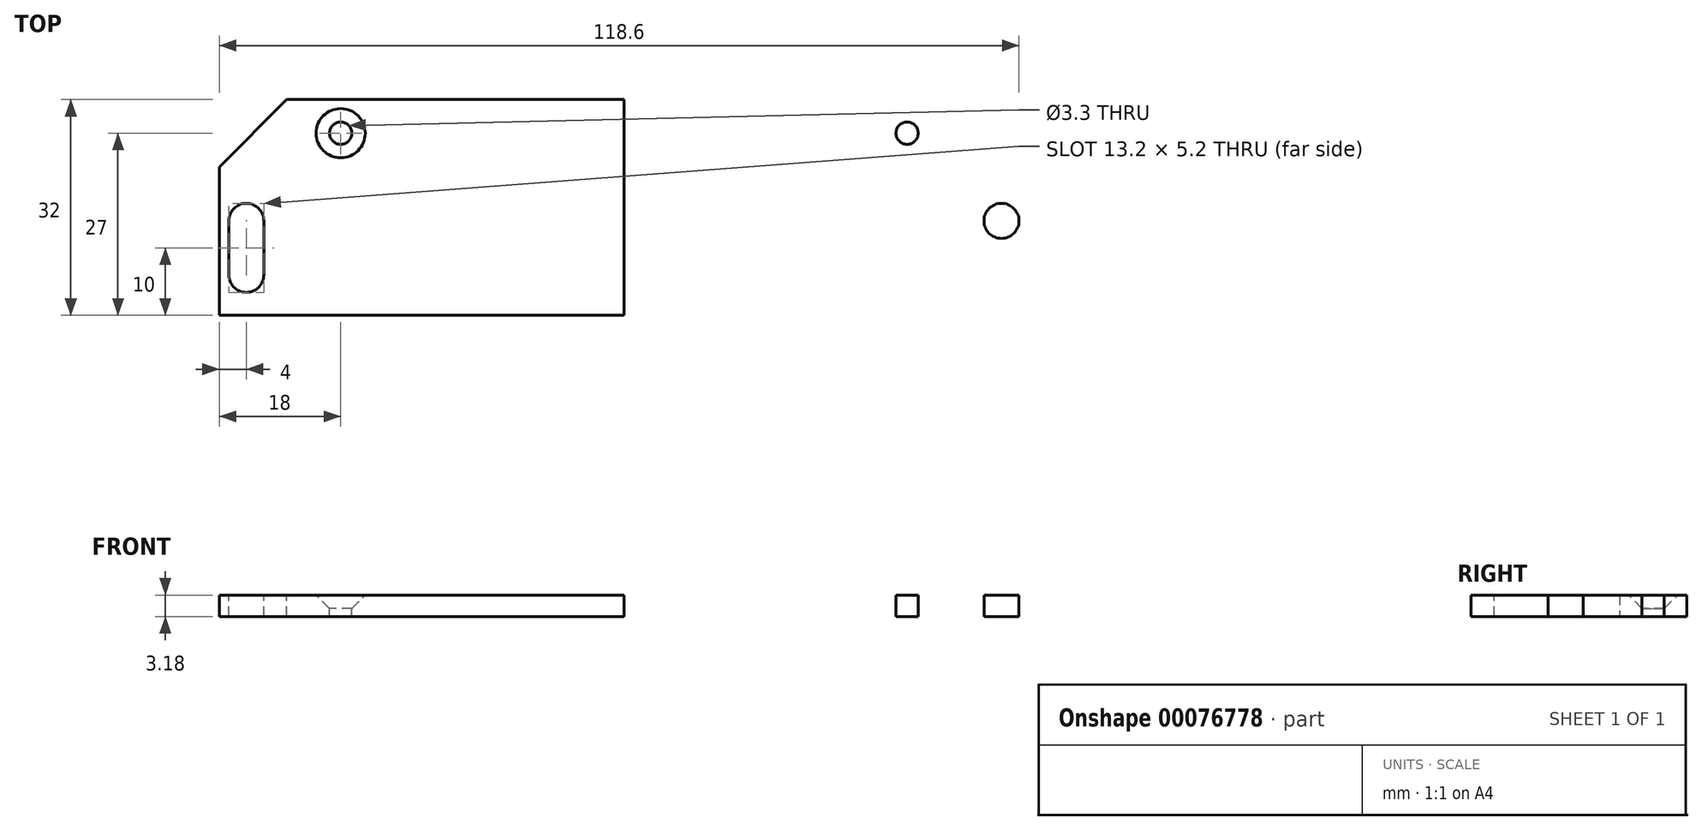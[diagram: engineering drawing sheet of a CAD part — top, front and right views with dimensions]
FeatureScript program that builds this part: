
annotation { "Feature Type Name" : "Feature", "Feature Type Description" : "" }
export const myFeature = defineFeature(function(context is Context, id is Id, definition is map)
    precondition{}
    {
        {
            var Q0;
            Q0=qCreatedBy(makeId("Top.planeOp"),FACE);
            var sketch = newSketch(context, id + "F0", { "sketchPlane" : qUnion([Q0])});
            skLineSegment(sketch, "E0.bottom", {"start": v(-60, 0) * mm, "end": v(60, 0) * mm});
            skLineSegment(sketch, "E0.top", {"start": v(-60, 32) * mm, "end": v(60, 32) * mm});
            skLineSegment(sketch, "E0.left", {"start": v(-60, 0) * mm, "end": v(-60, 32) * mm});
            skLineSegment(sketch, "E0.right", {"start": v(60, 0) * mm, "end": v(60, 32) * mm});
            skLineSegment(sketch, "E1", {"start": v(0, 0) * mm, "end": v(0, 32) * mm});
            skSolve(sketch);
        }
        {
            var Q0;
            {var subQ0=sQuery(id+"F0.wireOp",EDGE,"E0.left");Q0=makeQuery(id+"F0.imprint","IMPRINT",FACE,{"disambiguationData":[TD([[makeQuery(id+"F0.imprint","IMPRINT",EDGE,{"derivedFrom":subQ0}),-1.0]])]});}
            var Q1;
            {var subQ0=sQuery(id+"F0.wireOp",EDGE,"E0.right");Q1=makeQuery(id+"F0.imprint","IMPRINT",FACE,{"disambiguationData":[TD([[makeQuery(id+"F0.imprint","IMPRINT",EDGE,{"derivedFrom":subQ0}),1.0]])]});}
            extrude(context, id + "F1", {"entities" : qUnion([Q0, Q1]), "depth" : 3.17 * mm});
        }
        {
            var Q0;
            Q0=makeQuery(id+"F1.opExtrude","CAP_FACE",FACE,{"disambiguationData":[OSD([sQuery(id+"F0.wireOp",EDGE,"E0.bottom"),sQuery(id+"F0.wireOp",EDGE,"E0.top"),sQuery(id+"F0.wireOp",EDGE,"E0.left"),sQuery(id+"F0.wireOp",EDGE,"E0.right")])],"isStart":false});
            var sketch = newSketch(context, id + "F2", { "sketchPlane" : qUnion([Q0])});
            skLineSegment(sketch, "E2", {"start": v(0, 0) * mm, "end": v(0, 32) * mm});
            skCircle(sketch, "E3", {"center": v(-42, 27) * mm, "radius": 1.65 * mm});
            skCircle(sketch, "E4", {"center": v(-56, 14) * mm, "radius": 2.6 * mm});
            skCircle(sketch, "E5.MirrorC", {"center": v(42, 27) * mm, "radius": 1.65 * mm});
            skCircle(sketch, "E6.MirrorC", {"center": v(56, 14) * mm, "radius": 2.6 * mm});
            skCircle(sketch, "E7", {"center": v(-56, 6) * mm, "radius": 2.6 * mm});
            skLineSegment(sketch, "E8", {"start": v(-56, 14) * mm, "end": v(-58.6, 14) * mm});
            skLineSegment(sketch, "E9", {"start": v(-58.6, 14) * mm, "end": v(-58.6, 6) * mm});
            skLineSegment(sketch, "E10", {"start": v(-58.6, 6) * mm, "end": v(-53.4, 6) * mm});
            skLineSegment(sketch, "E11", {"start": v(-53.4, 6) * mm, "end": v(-53.4, 14) * mm});
            skCircle(sketch, "E12.MirrorC", {"center": v(56, 6) * mm, "radius": 2.6 * mm});
            skLineSegment(sketch, "E13.MirrorCS", {"start": v(58.6, 14) * mm, "end": v(58.6, 6) * mm});
            skLineSegment(sketch, "E14.MirrorCS", {"start": v(58.6, 6) * mm, "end": v(53.4, 6) * mm});
            skLineSegment(sketch, "E15.MirrorCS", {"start": v(53.4, 6) * mm, "end": v(53.4, 14) * mm});
            skLineSegment(sketch, "E16.MirrorCS", {"start": v(56, 14) * mm, "end": v(58.6, 14) * mm});
            skSolve(sketch);
        }
        {
            var Q0;
            Q0=makeQuery(id+"F2.imprint","IMPRINT",FACE,{"disambiguationData":[TD([[makeQuery(id+"F2.imprint","IMPRINT",EDGE,{"derivedFrom":sQuery(id+"F2.wireOp",EDGE,"E4")}),1.0]])]});
            var Q1;
            Q1=makeQuery(id+"F2.imprint","IMPRINT",FACE,{"disambiguationData":[TD([[makeQuery(id+"F2.imprint","IMPRINT",EDGE,{"derivedFrom":sQuery(id+"F2.wireOp",EDGE,"E3")}),1.0]])]});
            var Q2;
            Q2=makeQuery(id+"F2.imprint","IMPRINT",FACE,{"disambiguationData":[TD([[makeQuery(id+"F2.imprint","IMPRINT",EDGE,{"derivedFrom":sQuery(id+"F2.wireOp",EDGE,"E5.MirrorC")}),-1.0]])]});
            var Q3;
            Q3=makeQuery(id+"F2.imprint","IMPRINT",FACE,{"disambiguationData":[TD([[makeQuery(id+"F2.imprint","IMPRINT",EDGE,{"derivedFrom":sQuery(id+"F2.wireOp",EDGE,"E6.MirrorC")}),-1.0]])]});
            var Q4;
            {var subQ0=sQuery(id+"F2.wireOp",EDGE,"E9");Q4=makeQuery(id+"F2.imprint","IMPRINT",FACE,{"disambiguationData":[TD([[makeQuery(id+"F2.imprint","IMPRINT",EDGE,{"derivedFrom":subQ0}),1.0]])]});}
            var Q5;
            {var subQ0=sQuery(id+"F2.wireOp",EDGE,"E10");Q5=makeQuery(id+"F2.imprint","IMPRINT",FACE,{"disambiguationData":[TD([[makeQuery(id+"F2.imprint","IMPRINT",EDGE,{"derivedFrom":subQ0}),1.0]])]});}
            var Q6;
            {var subQ0=sQuery(id+"F2.wireOp",EDGE,"E10");Q6=makeQuery(id+"F2.imprint","IMPRINT",FACE,{"disambiguationData":[TD([[makeQuery(id+"F2.imprint","IMPRINT",EDGE,{"derivedFrom":subQ0}),-1.0]])]});}
            var Q7;
            {var subQ0=sQuery(id+"F2.wireOp",EDGE,"E13.MirrorCS");Q7=makeQuery(id+"F2.imprint","IMPRINT",FACE,{"disambiguationData":[TD([[makeQuery(id+"F2.imprint","IMPRINT",EDGE,{"derivedFrom":subQ0}),-1.0]])]});}
            var Q8;
            {var subQ0=sQuery(id+"F2.wireOp",EDGE,"E14.MirrorCS");Q8=makeQuery(id+"F2.imprint","IMPRINT",FACE,{"disambiguationData":[TD([[makeQuery(id+"F2.imprint","IMPRINT",EDGE,{"derivedFrom":subQ0}),-1.0]])]});}
            var Q9;
            {var subQ0=sQuery(id+"F2.wireOp",EDGE,"E14.MirrorCS");Q9=makeQuery(id+"F2.imprint","IMPRINT",FACE,{"disambiguationData":[TD([[makeQuery(id+"F2.imprint","IMPRINT",EDGE,{"derivedFrom":subQ0}),1.0]])]});}
            extrude(context, id + "F3", {"entities" : qUnion([Q0, Q1, Q2, Q3, Q4, Q5, Q6, Q7, Q8, Q9]), "operationType" : NewBodyOperationType.REMOVE, "endBound" : BoundingType.THROUGH_ALL, "oppositeDirection" : true, "depth" : 25 * mm});
        }
        {
            var Q0;
            Q0=makeQuery(id+"F3.boolean.opBoolean","COPY",EDGE,{"derivedFrom":makeQuery(id+"F3.opExtrude","CAP_EDGE",EDGE,{"disambiguationData":[OSD([sQuery(id+"F2.wireOp",EDGE,"E3")])],"isStart":true})});
            var Q1;
            Q1=makeQuery(id+"F3.boolean.opBoolean","COPY",EDGE,{"derivedFrom":makeQuery(id+"F3.opExtrude","CAP_EDGE",EDGE,{"disambiguationData":[OSD([sQuery(id+"F2.wireOp",EDGE,"E5.MirrorC")])],"isStart":true})});
            chamfer(context, id + "F4", {"entities" : qUnion([Q0, Q1]), "width" : 2 * mm, "tangentPropagation" : true});
        }
        {
            var Q0;
            Q0=makeQuery(id+"F1.opExtrude","SWEPT_EDGE",EDGE,{"disambiguationData":[OSD([sQuery(id+"F0.wireOp",EDGE,"E0.top"),sQuery(id+"F0.wireOp",EDGE,"E0.left")])]});
            var Q1;
            Q1=makeQuery(id+"F1.opExtrude","SWEPT_EDGE",EDGE,{"disambiguationData":[OSD([sQuery(id+"F0.wireOp",EDGE,"E0.top"),sQuery(id+"F0.wireOp",EDGE,"E0.right")])]});
            chamfer(context, id + "F5", {"entities" : qUnion([Q0, Q1]), "width" : 10 * mm, "tangentPropagation" : true});
        }
    });
